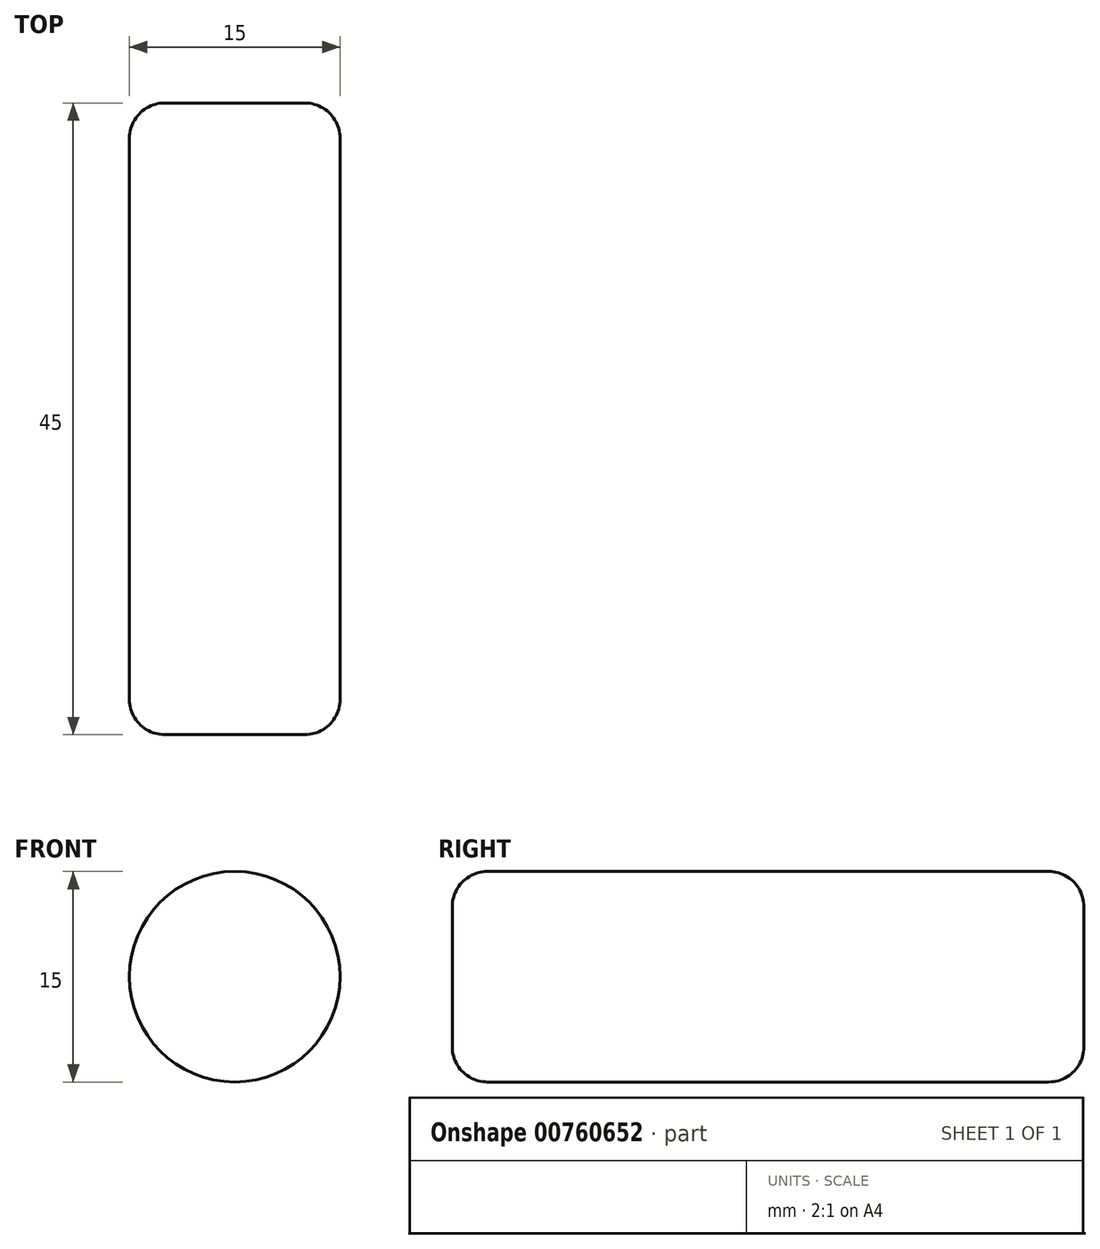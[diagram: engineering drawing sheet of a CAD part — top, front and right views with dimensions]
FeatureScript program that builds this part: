
annotation { "Feature Type Name" : "Feature", "Feature Type Description" : "" }
export const myFeature = defineFeature(function(context is Context, id is Id, definition is map)
    precondition{}
    {
        {
            var Q0;
            Q0=qCreatedBy(makeId("Front.planeOp"),FACE);
            var sketch = newSketch(context, id + "F0", { "sketchPlane" : qUnion([Q0])});
            skCircle(sketch, "E0", {"center": v(0, 0) * mm, "radius": 7.5 * mm});
            skSolve(sketch);
        }
        {
            var Q0;
            Q0 = qSketchRegion(id + "F0", true);
            extrude(context, id + "F1", {"entities" : qUnion([Q0]), "endBound" : BoundingType.SYMMETRIC, "depth" : 45 * mm, "offsetDistance" : 25 * mm});
        }
        {
            var Q0;
            Q0=makeQuery(id+"F1.opExtrude","CAP_FACE",FACE,{"disambiguationData":[OSD([sQuery(id+"F0.wireOp",EDGE,"E0")])],"isStart":false});
            var Q1;
            Q1=makeQuery(id+"F1.opExtrude","CAP_FACE",FACE,{"disambiguationData":[OSD([sQuery(id+"F0.wireOp",EDGE,"E0")])],"isStart":true});
            fillet(context, id + "F2", {"entities" : qUnion([Q0, Q1]), "radius" : 2.5 * mm, "tangentPropagation" : true, "allowEdgeOverflow" : false});
        }
    });
